# Revit family: LAMP_TRACE 200 IP65
name_source: partatom
category: Modelos genéricos
revit_build: Autodesk Revit 2015 (Build: 20140606_1530(x64)
units: mm (PartAtom-declared; Revit-internal decimal feet)

## types (3) — shared parameters
CRI = 80
Dimensions = 105 x 111 x 204
Elevación por defecto = 1219 mm
Fabricante = LAMP
Finish = Cataphoresis
Gear = Electronic
IEE = A++
Initial color = 3000 K
Installation instructions = https://www.lamp.es
Insulation class = I
LED Lifetime = 100.000 L90 B10
Lamp = MID-POWER LED
Last update = 13/11/2020
Luminaire type = Outdoor - Wall Mounted
MacAdam = <3
Manufacturer URL = http://www.lamp.es
Manufacturer country = Spain
Manufacturer name = LAMP
Photometric web file = Cuerpo Trace 200 : 92LM 3000 BLACK
Power Supply = 100-240V 50-60Hz
Product URL = https://www.lamp.es
Product datasheet = http://www.lamp.es
Protection rating = IP65 / IK07
Recessed dimensions = 107 x 135 x 212
Type = MID POWER OSRAM

## per-type parameters (varying)
| type | Descripción | Efficacy | Initial intensity | Modelo | Plum | Power | Product code | Weight |
| 92LM 3000 BLACK | TRACE IP65 200 HOR 70 WW BK. | 37 lm/W | 92 lm | TC120H0265AS830NB | 3 W | 1 W | TC120H0265AS830NB | 1.18 kg |
| 94LM 3000 BLACK | TRACE IP65 200 VERT 70 WW BK. | 38 lm/W | 94 lm | TC120V0265AS830NB | 3 W | 1 W | TC120V0265AS830NB | 1.18 kg |
| 156LM 3000 BLACK | TRACE IP65 200 VERT 120 WW BK. | 38 lm/W | 156 lm | TC120V0265SY830NB | 4 W | 3 W | TC120V0265SY830NB | 1.20 kg |
